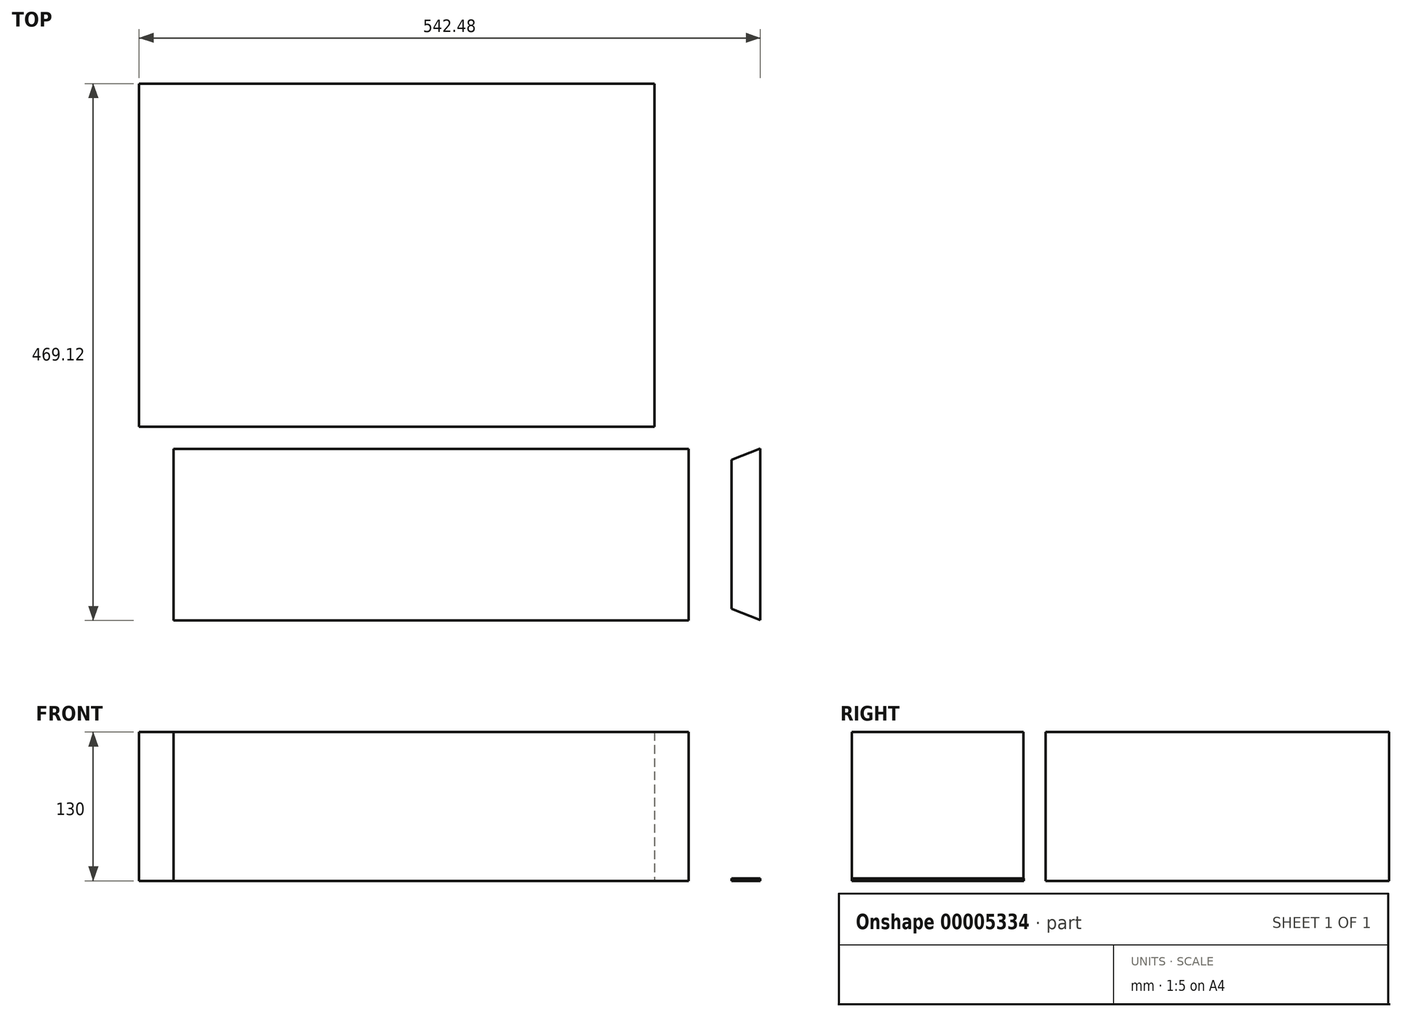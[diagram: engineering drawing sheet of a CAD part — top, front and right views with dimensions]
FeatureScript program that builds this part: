
annotation { "Feature Type Name" : "Feature", "Feature Type Description" : "" }
export const myFeature = defineFeature(function(context is Context, id is Id, definition is map)
    precondition{}
    {
        {
            var Q0;
            Q0=qCreatedBy(makeId("Top.planeOp"),FACE);
            var sketch = newSketch(context, id + "F0", { "sketchPlane" : qUnion([Q0])});
            skLineSegment(sketch, "E0.rect.bottom", {"start": v(225, 75) * mm, "end": v(-225, 75) * mm});
            skLineSegment(sketch, "E0.rect.top", {"start": v(225, -75) * mm, "end": v(-225, -75) * mm});
            skLineSegment(sketch, "E0.rect.left", {"start": v(225, 75) * mm, "end": v(225, -75) * mm});
            skLineSegment(sketch, "E0.rect.right", {"start": v(-225, 75) * mm, "end": v(-225, -75) * mm});
            skPoint(sketch, "E0.rect.middle", {"position": v(0, 0) * mm});
            skSolve(sketch);
        }
        {
            var Q0;
            Q0 = qSketchRegion(id + "F0", true);
            extrude(context, id + "F1", {"entities" : qUnion([Q0]), "depth" : 130 * mm});
        }
        {
            var Q0;
            Q0=qCreatedBy(makeId("Top.planeOp"),FACE);
            var sketch = newSketch(context, id + "F2", { "sketchPlane" : qUnion([Q0])});
            skLineSegment(sketch, "E1.bottom", {"start": v(-255, 94.12) * mm, "end": v(195, 94.12) * mm});
            skLineSegment(sketch, "E1.top", {"start": v(-255, 394.12) * mm, "end": v(195, 394.12) * mm});
            skLineSegment(sketch, "E1.left", {"start": v(-255, 94.12) * mm, "end": v(-255, 394.12) * mm});
            skLineSegment(sketch, "E1.right", {"start": v(195, 94.12) * mm, "end": v(195, 394.12) * mm});
            skSolve(sketch);
        }
        {
            var Q0;
            Q0=makeQuery(id+"F2.imprint","IMPRINT",FACE,{"disambiguationData":[TD([[makeQuery(id+"F2.imprint","IMPRINT",EDGE,{"derivedFrom":sQuery(id+"F2.wireOp",EDGE,"E1.bottom")}),1.0]])]});
            extrude(context, id + "F3", {"entities" : qUnion([Q0]), "depth" : 130 * mm});
        }
        {
            var Q0;
            Q0=qCreatedBy(makeId("Top.planeOp"),FACE);
            var sketch = newSketch(context, id + "F4", { "sketchPlane" : qUnion([Q0])});
            skLineSegment(sketch, "E2", {"start": v(287.49, 75.22) * mm, "end": v(262.49, 65.22) * mm});
            skLineSegment(sketch, "E3", {"start": v(262.49, -64.78) * mm, "end": v(262.49, 65.22) * mm});
            skLineSegment(sketch, "E4", {"start": v(262.49, -64.78) * mm, "end": v(287.49, -74.78) * mm});
            skLineSegment(sketch, "E5", {"start": v(287.49, -74.78) * mm, "end": v(287.49, 75.22) * mm});
            skSolve(sketch);
        }
        {
            var Q0;
            Q0 = qSketchRegion(id + "F4", true);
            extrude(context, id + "F5", {"entities" : qUnion([Q0]), "operationType" : NewBodyOperationType.ADD, "depth" : 2 * mm});
        }
    });
